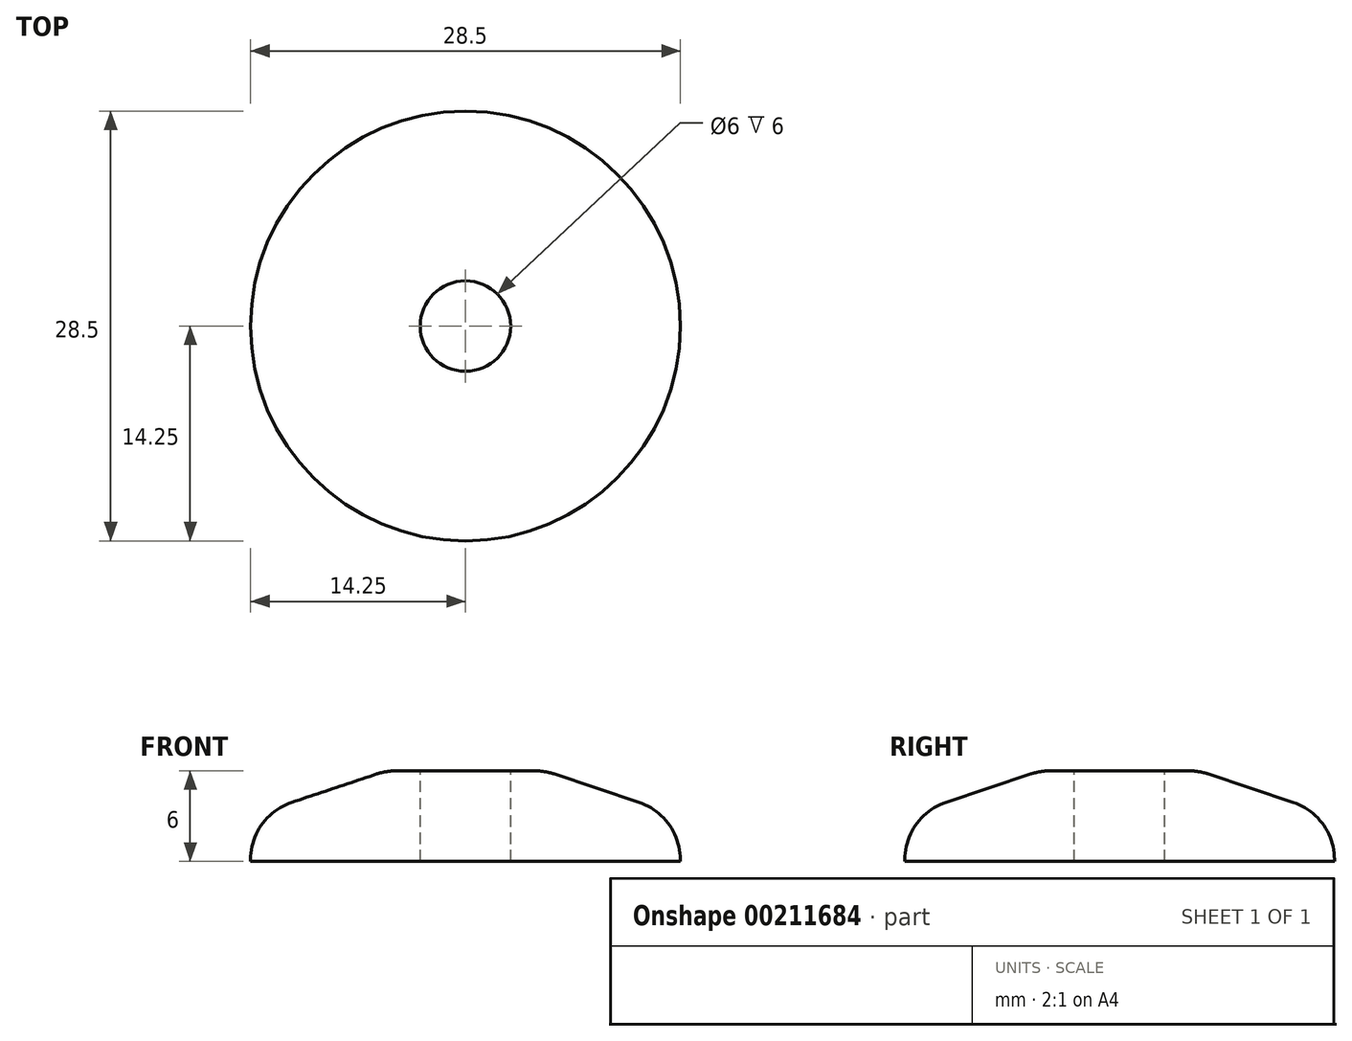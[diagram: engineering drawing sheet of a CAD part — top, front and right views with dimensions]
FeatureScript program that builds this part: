
annotation { "Feature Type Name" : "Feature", "Feature Type Description" : "" }
export const myFeature = defineFeature(function(context is Context, id is Id, definition is map)
    precondition{}
    {
        {
            var Q0;
            Q0=qCreatedBy(makeId("Top.planeOp"),FACE);
            var sketch = newSketch(context, id + "F0", { "sketchPlane" : qUnion([Q0])});
            skCircle(sketch, "E0", {"center": v(0, 0) * mm, "radius": 14.25 * mm});
            skSolve(sketch);
        }
        {
            var Q0;
            Q0=makeQuery(id+"F0.imprint","IMPRINT",FACE,{"disambiguationData":[TD([[makeQuery(id+"F0.imprint","IMPRINT",EDGE,{"derivedFrom":sQuery(id+"F0.wireOp",EDGE,"E0")}),1.0]])]});
            extrude(context, id + "F1", {"entities" : qUnion([Q0]), "depth" : 6 * mm});
        }
        {
            var Q0;
            Q0=makeQuery(id+"F1.opExtrude","CAP_FACE",FACE,{"disambiguationData":[OSD([sQuery(id+"F0.wireOp",EDGE,"E0")])],"isStart":false});
            var sketch = newSketch(context, id + "F2", { "sketchPlane" : qUnion([Q0])});
            skCircle(sketch, "E1", {"center": v(0, 0) * mm, "radius": 3 * mm});
            skSolve(sketch);
        }
        {
            var Q0;
            Q0=makeQuery(id+"F2.imprint","IMPRINT",FACE,{"disambiguationData":[TD([[makeQuery(id+"F2.imprint","IMPRINT",EDGE,{"derivedFrom":sQuery(id+"F2.wireOp",EDGE,"E1")}),1.0]])]});
            extrude(context, id + "F3", {"entities" : qUnion([Q0]), "operationType" : NewBodyOperationType.REMOVE, "oppositeDirection" : true, "depth" : 25 * mm});
        }
        {
            var Q0;
            Q0=makeQuery(id+"F1.opExtrude","CAP_EDGE",EDGE,{"disambiguationData":[OSD([sQuery(id+"F0.wireOp",EDGE,"E0")])],"isStart":false});
            chamfer(context, id + "F4", {"entities" : qUnion([Q0]), "chamferType" : ChamferType.TWO_OFFSETS, "width1" : 9 * mm, "oppositeDirection" : false, "width2" : 3 * mm, "tangentPropagation" : true});
        }
        {
            var Q0;
            {var subQ0=sQuery(id+"F0.wireOp",EDGE,"E0");Q0=makeQuery(id+"F4.opChamfer","BLEND_EDGE",EDGE,{"blendedFrom":[makeQuery(id+"F1.opExtrude","CAP_EDGE",EDGE,{"disambiguationData":[OSD([subQ0])],"isStart":false}),makeQuery(id+"F1.opExtrude","CAP_FACE",FACE,{"disambiguationData":[OSD([subQ0])],"isStart":false})],"blendedInto":[makeQuery(id+"F1.opExtrude","CAP_FACE",FACE,{"disambiguationData":[OSD([subQ0])],"isStart":false})]});}
            var Q1;
            {var subQ0=sQuery(id+"F0.wireOp",EDGE,"E0");Q1=makeQuery(id+"F4.opChamfer","BLEND_EDGE",EDGE,{"blendedFrom":[makeQuery(id+"F1.opExtrude","CAP_EDGE",EDGE,{"disambiguationData":[OSD([subQ0])],"isStart":false}),makeQuery(id+"F1.opExtrude","SWEPT_FACE",FACE,{"disambiguationData":[OSD([subQ0])]})],"blendedInto":[makeQuery(id+"F1.opExtrude","SWEPT_FACE",FACE,{"disambiguationData":[OSD([subQ0])]})]});}
            fillet(context, id + "F5", {"entities" : qUnion([Q0, Q1]), "radius" : 4 * mm, "tangentPropagation" : true, "allowEdgeOverflow" : false});
        }
    });
